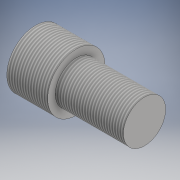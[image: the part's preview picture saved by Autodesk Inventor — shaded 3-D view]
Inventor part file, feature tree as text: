
AUTODESK INVENTOR PART (.ipt)
format: ipt  version: 2017 (Build 210142000, 142)  size: 121,856 bytes
history: native  units: mm
features: sketch x5, extrude x2, thread x2
ambient origin geometry x8: Origin, YZ Plane, XZ Plane, XY Plane, X Axis, Y Axis, Z Axis, Center Point
bodies: Solid1 (feature_tree)
feature tree (9):
  extrude  "Extrusion1"  Depth=10.0mm TaperAngle=0.0deg
  thread  "Thread1"  [1 undecoded]
  sketch  "Sketch2"  dims[d6=10.0mm d7=0.0mm]
  extrude  "Extrusion2"  [1 undecoded]
  sketch  "Sketch4"
  sketch  "Sketch5"
  thread  "Thread2"  [1 undecoded]
  sketch  "Sketch1"  dims[d0=25.0mm d1=0.0mm d2=10.0mm d3=0.0mm d4=15.0mm d5=0.0mm]
  sketch  "Sketch3"
note: 3 required parameter values undecoded (feature->parameter linkage not recoverable at this tier; creation-order binding heuristic only, values carry confidence <= 0.55)
